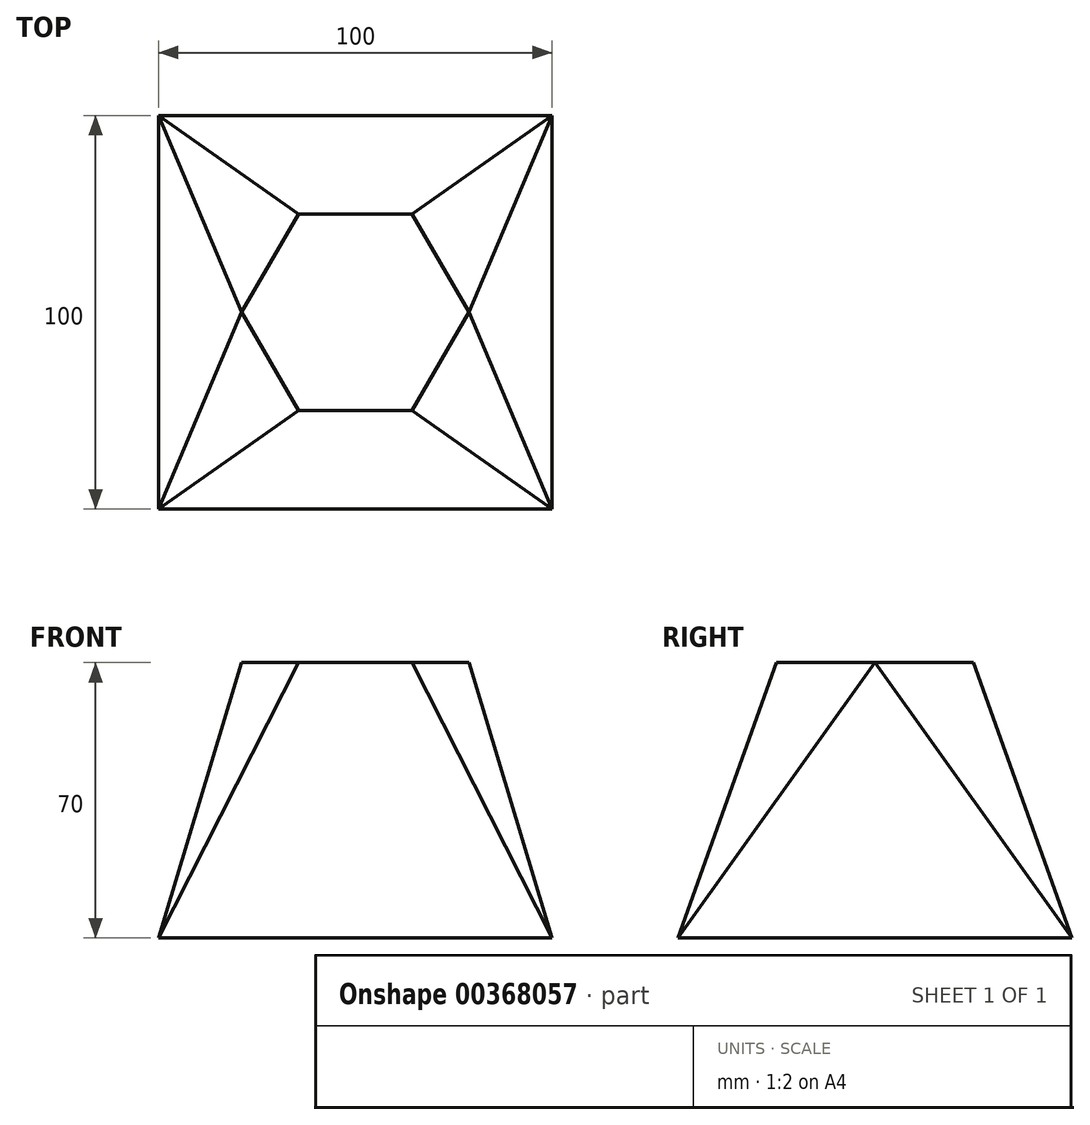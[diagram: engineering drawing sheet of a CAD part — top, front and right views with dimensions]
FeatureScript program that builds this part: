
annotation { "Feature Type Name" : "Feature", "Feature Type Description" : "" }
export const myFeature = defineFeature(function(context is Context, id is Id, definition is map)
    precondition{}
    {
        {
            var Q0;
            Q0=qCreatedBy(makeId("Top.planeOp"),FACE);
            var sketch = newSketch(context, id + "F0", { "sketchPlane" : qUnion([Q0])});
            skLineSegment(sketch, "E0.bottom", {"start": v(50, 50) * mm, "end": v(-50, 50) * mm});
            skLineSegment(sketch, "E0.top", {"start": v(50, -50) * mm, "end": v(-50, -50) * mm});
            skLineSegment(sketch, "E0.left", {"start": v(50, 50) * mm, "end": v(50, -50) * mm});
            skLineSegment(sketch, "E0.right", {"start": v(-50, 50) * mm, "end": v(-50, -50) * mm});
            skPoint(sketch, "E0.middle", {"position": v(0, 0) * mm});
            skSolve(sketch);
        }
        {
            var Q0;
            Q0=qCreatedBy(makeId("Top.planeOp"),FACE);
            cPlane(context, id + "F1", {"entities" : qUnion([Q0]), "cplaneType" : CPlaneType.OFFSET, "offset" : 70 * mm, "width" : 150 * mm, "height" : 150 * mm});
        }
        {
            var Q0;
            Q0=qCreatedBy(id+"F1.planeOp",FACE);
            var sketch = newSketch(context, id + "F2", { "sketchPlane" : qUnion([Q0])});
            skCircle(sketch, "E1.cCircle", {"center": v(0, 0) * mm, "radius": 25 * mm, "construction": true});
            skLineSegment(sketch, "E1.0", {"start": v(14.43, -25) * mm, "end": v(-14.43, -25) * mm});
            skLineSegment(sketch, "E1.1", {"start": v(-14.43, -25) * mm, "end": v(-28.87, 0) * mm});
            skLineSegment(sketch, "E1.2", {"start": v(-28.87, 0) * mm, "end": v(-14.43, 25) * mm});
            skLineSegment(sketch, "E1.3", {"start": v(-14.43, 25) * mm, "end": v(14.43, 25) * mm});
            skLineSegment(sketch, "E1.4", {"start": v(14.43, 25) * mm, "end": v(28.87, 0) * mm});
            skLineSegment(sketch, "E1.5", {"start": v(28.87, 0) * mm, "end": v(14.43, -25) * mm});
            skPoint(sketch, "E1.0.midPoint", {"position": v(0, -25) * mm});
            skLineSegment(sketch, "E2", {"start": v(-14.43, 25) * mm, "end": v(-14.43, -25) * mm});
            skLineSegment(sketch, "E3", {"start": v(14.43, 25) * mm, "end": v(14.43, -25) * mm});
            skSolve(sketch);
        }
        {
            var Q0;
            Q0=makeQuery(id+"F2.imprint","IMPRINT",FACE,{"disambiguationData":[TD([[makeQuery(id+"F2.imprint","IMPRINT",EDGE,{"derivedFrom":sQuery(id+"F2.wireOp",EDGE,"E1.0")}),-1.0]])]});
            var Q1;
            Q1=makeQuery(id+"F0.imprint","IMPRINT",FACE,{"disambiguationData":[TD([[makeQuery(id+"F0.imprint","IMPRINT",EDGE,{"derivedFrom":sQuery(id+"F0.wireOp",EDGE,"E0.bottom")}),1.0]])]});
            loft(context, id + "F3", {"sheetProfilesArray" : [{ "sheetProfileEntities" : qUnion([Q0]) }, { "sheetProfileEntities" : qUnion([Q1]) }]});
        }
        {
            var Q1;
            Q1=makeQuery(id+"F2.imprint","IMPRINT",FACE,{"disambiguationData":[TD([[makeQuery(id+"F2.imprint","IMPRINT",EDGE,{"derivedFrom":sQuery(id+"F2.wireOp",EDGE,"E1.4")}),-1.0]])]});
            var Q2;
            Q2=makeQuery(id+"F3.opLoft","MID_CAP_VERTEX",VERTEX,{"disambiguationData":[OSD([sQuery(id+"F0.wireOp",EDGE,"E0.top"),sQuery(id+"F0.wireOp",EDGE,"E0.left")])],"capPos":1.0});
            loft(context, id + "F4", {"operationType" : NewBodyOperationType.ADD, "sheetProfilesArray" : [{ "sheetProfileEntities" : qUnion([Q1]) }, { "sheetProfileEntities" : qUnion([Q2]) }]});
        }
        {
            var Q1;
            Q1=makeQuery(id+"F2.imprint","IMPRINT",FACE,{"disambiguationData":[TD([[makeQuery(id+"F2.imprint","IMPRINT",EDGE,{"derivedFrom":sQuery(id+"F2.wireOp",EDGE,"E1.4")}),-1.0]])]});
            var Q2;
            Q2=makeQuery(id+"F3.opLoft","MID_CAP_VERTEX",VERTEX,{"disambiguationData":[OSD([sQuery(id+"F0.wireOp",EDGE,"E0.bottom"),sQuery(id+"F0.wireOp",EDGE,"E0.left")])],"capPos":1.0});
            loft(context, id + "F5", {"operationType" : NewBodyOperationType.ADD, "sheetProfilesArray" : [{ "sheetProfileEntities" : qUnion([Q1]) }, { "sheetProfileEntities" : qUnion([Q2]) }]});
        }
        {
            var Q1;
            Q1=makeQuery(id+"F4.opLoft","SWEPT_FACE",FACE,{"disambiguationData":[OSD([sQuery(id+"F2.wireOp",EDGE,"E1.3"),sQuery(id+"F2.wireOp",EDGE,"E1.4"),sQuery(id+"F2.wireOp",EDGE,"E1.5"),sQuery(id+"F2.wireOp",EDGE,"E3")])]});
            var Q2;
            Q2=makeQuery(id+"F5.opLoft","SWEPT_FACE",FACE,{"disambiguationData":[OSD([sQuery(id+"F2.wireOp",EDGE,"E1.0"),sQuery(id+"F2.wireOp",EDGE,"E1.4"),sQuery(id+"F2.wireOp",EDGE,"E1.5"),sQuery(id+"F2.wireOp",EDGE,"E3")])]});
            var Q3;
            {var subQ0=sQuery(id+"F0.wireOp",EDGE,"E0.left");var subQ1=sQuery(id+"F0.wireOp",EDGE,"E0.top");Q3=makeQuery(id+"F4.boolean.opBoolean","MERGE",VERTEX,{"derivedFrom":[makeQuery(id+"F3.opLoft","MID_CAP_VERTEX",VERTEX,{"disambiguationData":[OSD([subQ1,subQ0])],"capPos":1.0}),makeQuery(id+"F4.opLoft","SWEPT_VERTEX",VERTEX,{"disambiguationData":[OSD([subQ1,subQ0,sQuery(id+"F2.wireOp",EDGE,"E1.3"),sQuery(id+"F2.wireOp",EDGE,"E1.4"),sQuery(id+"F2.wireOp",EDGE,"E3")])]})]});}
            var Q4;
            {var subQ0=sQuery(id+"F0.wireOp",EDGE,"E0.left");var subQ1=sQuery(id+"F0.wireOp",EDGE,"E0.bottom");Q4=makeQuery(id+"F5.boolean.opBoolean","MERGE",VERTEX,{"derivedFrom":[makeQuery(id+"F3.opLoft","MID_CAP_VERTEX",VERTEX,{"disambiguationData":[OSD([subQ1,subQ0])],"capPos":1.0}),makeQuery(id+"F5.opLoft","SWEPT_VERTEX",VERTEX,{"disambiguationData":[OSD([subQ1,subQ0,sQuery(id+"F2.wireOp",EDGE,"E1.3"),sQuery(id+"F2.wireOp",EDGE,"E1.4"),sQuery(id+"F2.wireOp",EDGE,"E3")])]})]});}
            loft(context, id + "F6", {"operationType" : NewBodyOperationType.ADD, "sheetProfilesArray" : [{ "sheetProfileEntities" : qUnion([Q1]) }, { "sheetProfileEntities" : qUnion([Q2]) }], "matchConnections" : true, "connections" : [{ "connectionEntities" : qUnion([Q3, Q4]), "connectionEdgeQueries" : qUnion([]), "connectionEdgeParameters" : [] }]});
        }
        {
            var Q1;
            Q1=makeQuery(id+"F2.imprint","IMPRINT",FACE,{"disambiguationData":[TD([[makeQuery(id+"F2.imprint","IMPRINT",EDGE,{"derivedFrom":sQuery(id+"F2.wireOp",EDGE,"E1.1")}),-1.0]])]});
            var Q2;
            Q2=makeQuery(id+"F3.opLoft","MID_CAP_VERTEX",VERTEX,{"disambiguationData":[OSD([sQuery(id+"F0.wireOp",EDGE,"E0.bottom"),sQuery(id+"F0.wireOp",EDGE,"E0.right")])],"capPos":1.0});
            loft(context, id + "F7", {"operationType" : NewBodyOperationType.ADD, "sheetProfilesArray" : [{ "sheetProfileEntities" : qUnion([Q1]) }, { "sheetProfileEntities" : qUnion([Q2]) }]});
        }
        {
            var Q1;
            Q1=makeQuery(id+"F2.imprint","IMPRINT",FACE,{"disambiguationData":[TD([[makeQuery(id+"F2.imprint","IMPRINT",EDGE,{"derivedFrom":sQuery(id+"F2.wireOp",EDGE,"E1.1")}),-1.0]])]});
            var Q2;
            Q2=makeQuery(id+"F3.opLoft","MID_CAP_VERTEX",VERTEX,{"disambiguationData":[OSD([sQuery(id+"F0.wireOp",EDGE,"E0.top"),sQuery(id+"F0.wireOp",EDGE,"E0.right")])],"capPos":1.0});
            loft(context, id + "F8", {"operationType" : NewBodyOperationType.ADD, "sheetProfilesArray" : [{ "sheetProfileEntities" : qUnion([Q1]) }, { "sheetProfileEntities" : qUnion([Q2]) }]});
        }
        {
            var Q1;
            Q1=makeQuery(id+"F7.opLoft","SWEPT_FACE",FACE,{"disambiguationData":[OSD([sQuery(id+"F2.wireOp",EDGE,"E1.0"),sQuery(id+"F2.wireOp",EDGE,"E1.1"),sQuery(id+"F2.wireOp",EDGE,"E1.2"),sQuery(id+"F2.wireOp",EDGE,"E2")])]});
            var Q2;
            Q2=makeQuery(id+"F8.opLoft","SWEPT_FACE",FACE,{"disambiguationData":[OSD([sQuery(id+"F2.wireOp",EDGE,"E1.1"),sQuery(id+"F2.wireOp",EDGE,"E1.2"),sQuery(id+"F2.wireOp",EDGE,"E1.3"),sQuery(id+"F2.wireOp",EDGE,"E2")])]});
            var Q3;
            {var subQ0=sQuery(id+"F0.wireOp",EDGE,"E0.right");var subQ1=sQuery(id+"F0.wireOp",EDGE,"E0.bottom");Q3=makeQuery(id+"F7.boolean.opBoolean","MERGE",VERTEX,{"derivedFrom":[makeQuery(id+"F3.opLoft","MID_CAP_VERTEX",VERTEX,{"disambiguationData":[OSD([subQ1,subQ0])],"capPos":1.0}),makeQuery(id+"F7.opLoft","SWEPT_VERTEX",VERTEX,{"disambiguationData":[OSD([subQ1,subQ0,sQuery(id+"F2.wireOp",EDGE,"E1.1"),sQuery(id+"F2.wireOp",EDGE,"E1.2")])]})]});}
            var Q4;
            {var subQ0=sQuery(id+"F0.wireOp",EDGE,"E0.right");var subQ1=sQuery(id+"F0.wireOp",EDGE,"E0.top");Q4=makeQuery(id+"F8.boolean.opBoolean","MERGE",VERTEX,{"derivedFrom":[makeQuery(id+"F3.opLoft","MID_CAP_VERTEX",VERTEX,{"disambiguationData":[OSD([subQ1,subQ0])],"capPos":1.0}),makeQuery(id+"F8.opLoft","SWEPT_VERTEX",VERTEX,{"disambiguationData":[OSD([subQ1,subQ0,sQuery(id+"F2.wireOp",EDGE,"E1.1"),sQuery(id+"F2.wireOp",EDGE,"E1.2")])]})]});}
            loft(context, id + "F9", {"operationType" : NewBodyOperationType.ADD, "sheetProfilesArray" : [{ "sheetProfileEntities" : qUnion([Q1]) }, { "sheetProfileEntities" : qUnion([Q2]) }], "matchConnections" : true, "connections" : [{ "connectionEntities" : qUnion([Q3, Q4]), "connectionEdgeQueries" : qUnion([]), "connectionEdgeParameters" : [] }]});
        }
    });
